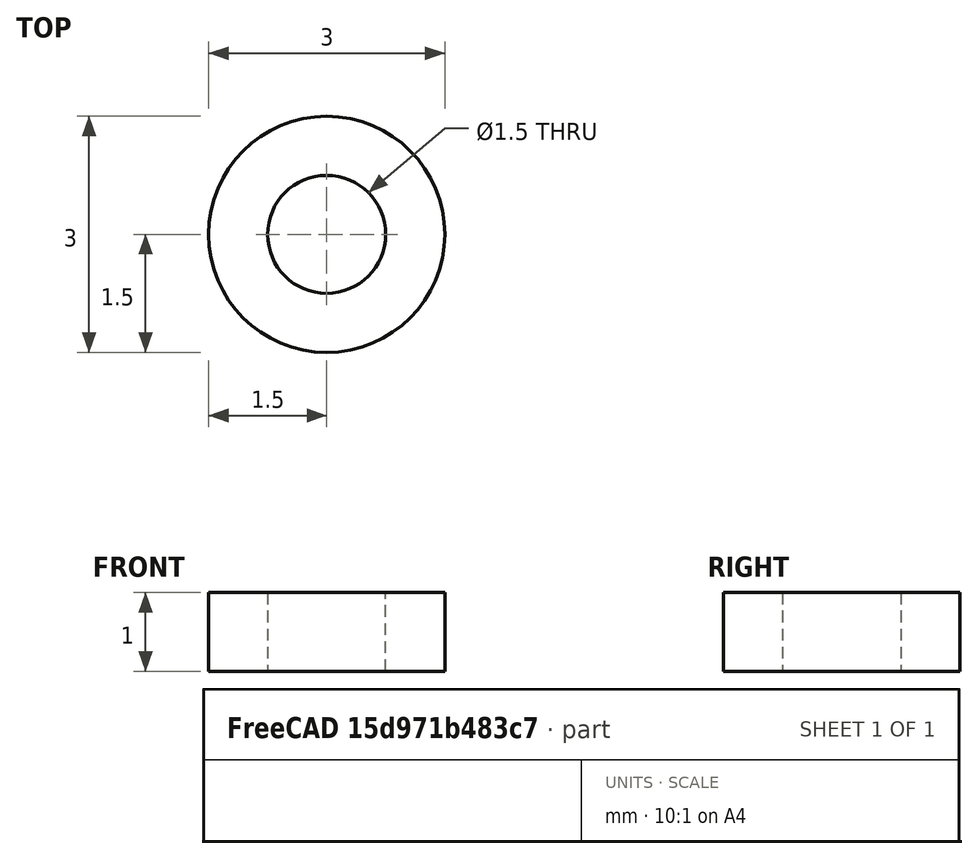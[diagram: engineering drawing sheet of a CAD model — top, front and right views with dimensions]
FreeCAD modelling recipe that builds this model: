
FCSTD DOCUMENT  (FreeCAD 0.18.1R)
Label: Entretoise_Pignion_Intermediaire
License: All rights reserved
LicenseURL: http://en.wikipedia.org/wiki/All_rights_reserved
objects: Sketcher::SketchObject×1, PartDesign::Pad×1, PartDesign::Body×1
note: 4 computed .brp shape members not serialized (recipe doc carries the construction recipe); baked Part::Feature solids carry a one-line shape summary decoded from their .brp

FEATURE [Sketcher::SketchObject] Sketch
  MapMode = 5
  Support = -> [XY_Plane]
  sketch-geometry (2):
    g0: Circle CenterX=0 CenterY=0 CenterZ=0 NormalX=0 NormalY=0 NormalZ=1 AngleXU=0 Radius=0.75
    g1: Circle CenterX=0 CenterY=0 CenterZ=0 NormalX=0 NormalY=0 NormalZ=1 AngleXU=0 Radius=1.5
  constraints (4):
    c: Coincident(g0,g-1)
    c: Coincident(g1,g0)
    c: Radius(g0) = 0.75
    c: Radius(g1) = 1.5
FEATURE [PartDesign::Pad] Pad
  Length = 1
  Length2 = 100
  Profile = -> Sketch
  Type = 0
FEATURE [PartDesign::Body] Body
  Group = -> [Sketch,Pad]
  Origin = -> Origin
  Tip = -> Pad
